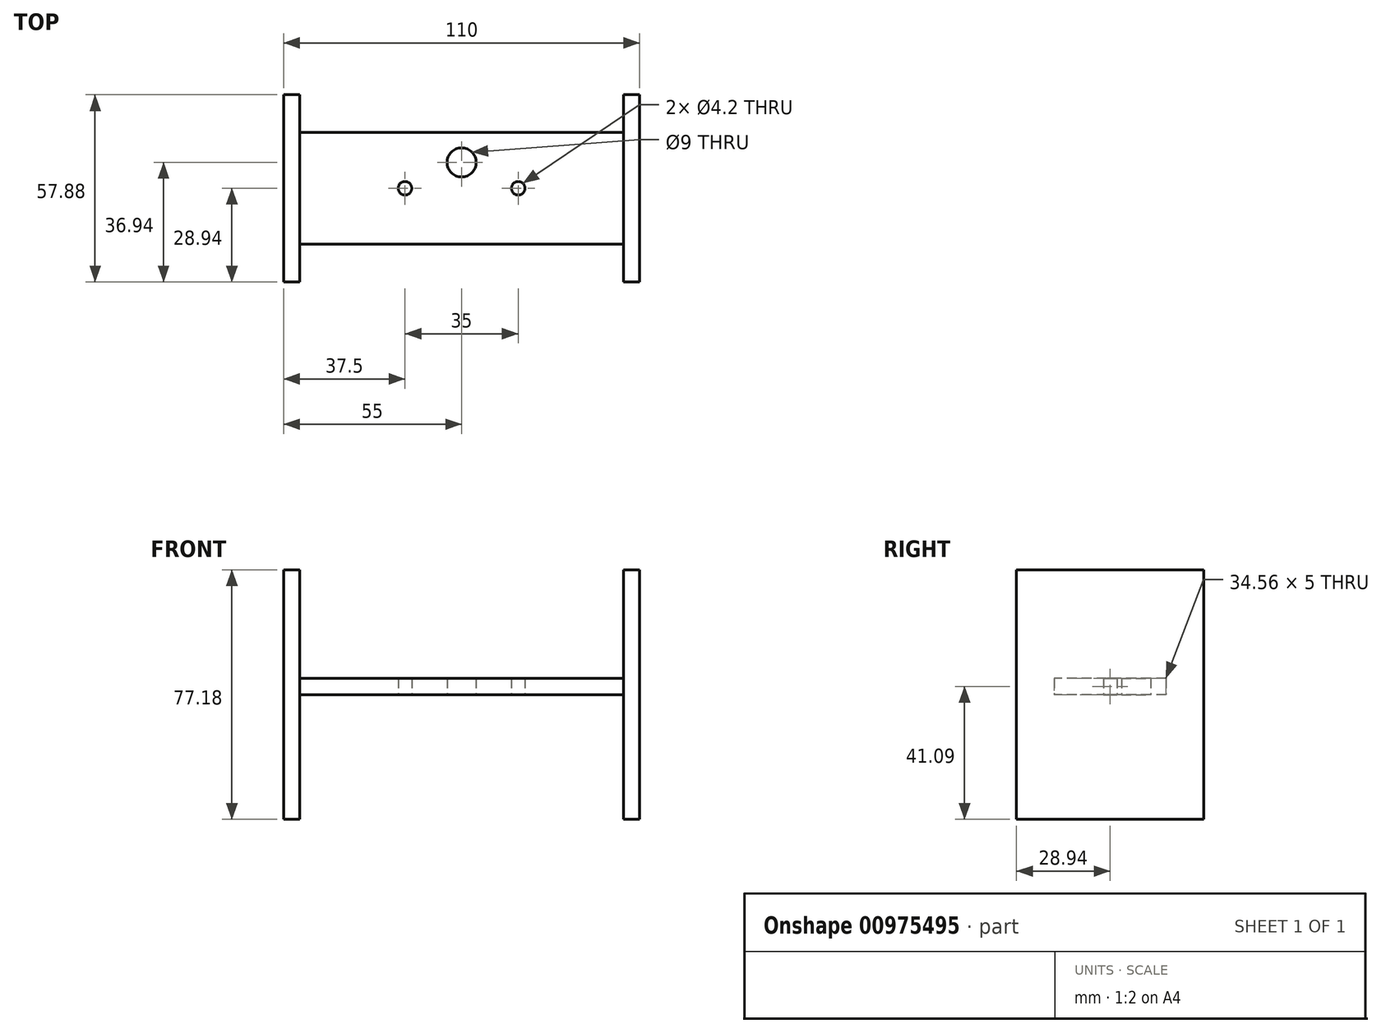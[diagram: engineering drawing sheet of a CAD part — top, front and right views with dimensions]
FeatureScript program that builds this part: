
annotation { "Feature Type Name" : "Feature", "Feature Type Description" : "" }
export const myFeature = defineFeature(function(context is Context, id is Id, definition is map)
    precondition{}
    {
        {
            var Q0;
            Q0=qCreatedBy(makeId("Top.planeOp"),FACE);
            var sketch = newSketch(context, id + "F0", { "sketchPlane" : qUnion([Q0])});
            skLineSegment(sketch, "E0.bottom", {"start": v(50, 17.28) * mm, "end": v(-50, 17.28) * mm});
            skLineSegment(sketch, "E0.top", {"start": v(50, -17.28) * mm, "end": v(-50, -17.28) * mm});
            skLineSegment(sketch, "E0.left", {"start": v(50, 17.28) * mm, "end": v(50, 12.28) * mm});
            skLineSegment(sketch, "E0.right", {"start": v(-50, 17.28) * mm, "end": v(-50, 12.28) * mm});
            skPoint(sketch, "E0.middle", {"position": v(0, 0) * mm});
            skLineSegment(sketch, "E1.bottom", {"start": v(55, -12.28) * mm, "end": v(50, -12.28) * mm});
            skLineSegment(sketch, "E1.top", {"start": v(55, 12.28) * mm, "end": v(50, 12.28) * mm});
            skLineSegment(sketch, "E1.left", {"start": v(55, -12.28) * mm, "end": v(55, 12.28) * mm});
            skPoint(sketch, "E1.middle", {"position": v(50, 0) * mm});
            skPoint(sketch, "E2.orphan", {"position": v(45, 12.28) * mm});
            skLineSegment(sketch, "E3.trimOffspring", {"start": v(50, -12.28) * mm, "end": v(50, -17.28) * mm});
            skPoint(sketch, "E4.orphan", {"position": v(45, -12.28) * mm});
            skLineSegment(sketch, "E5.MirrorCS", {"start": v(-55, 12.28) * mm, "end": v(-50, 12.28) * mm});
            skLineSegment(sketch, "E6.MirrorCS", {"start": v(-55, -12.28) * mm, "end": v(-55, 12.28) * mm});
            skLineSegment(sketch, "E7.MirrorCS", {"start": v(-55, -12.28) * mm, "end": v(-50, -12.28) * mm});
            skLineSegment(sketch, "E8.trimOffspring", {"start": v(-50, -12.28) * mm, "end": v(-50, -17.28) * mm});
            skCircle(sketch, "E9", {"center": v(17.5, 0) * mm, "radius": 2.1 * mm});
            skCircle(sketch, "E10.MirrorC", {"center": v(-17.5, 0) * mm, "radius": 2.1 * mm});
            skCircle(sketch, "E11", {"center": v(0, 8) * mm, "radius": 4.5 * mm});
            skSolve(sketch);
        }
        {
            var Q0;
            Q0=makeQuery(id+"F0.imprint","IMPRINT",FACE,{"disambiguationData":[TD([[makeQuery(id+"F0.imprint","IMPRINT",EDGE,{"derivedFrom":sQuery(id+"F0.wireOp",EDGE,"E0.bottom")}),1.0]])]});
            extrude(context, id + "F1", {"entities" : qUnion([Q0]), "depth" : 5 * mm, "offsetDistance" : 25 * mm});
        }
        {
            var Q0;
            Q0=makeQuery(id+"F1.opExtrude","SWEPT_FACE",FACE,{"disambiguationData":[OSD([sQuery(id+"F0.wireOp",EDGE,"E1.left")])]});
            cPlane(context, id + "F2", {"entities" : qUnion([Q0]), "cplaneType" : CPlaneType.OFFSET, "offset" : 0 * mm, "width" : 150 * mm, "height" : 150 * mm});
        }
        {
            var Q0;
            Q0=qCreatedBy(id+"F2.planeOp",FACE);
            var sketch = newSketch(context, id + "F3", { "sketchPlane" : qUnion([Q0])});
            skLineSegment(sketch, "E12.bottom", {"start": v(28.94, -38.6) * mm, "end": v(-28.94, -38.6) * mm});
            skLineSegment(sketch, "E12.top", {"start": v(28.94, 38.6) * mm, "end": v(-28.94, 38.6) * mm});
            skLineSegment(sketch, "E12.left", {"start": v(28.94, -38.6) * mm, "end": v(28.94, 38.6) * mm});
            skLineSegment(sketch, "E12.right", {"start": v(-28.94, -38.6) * mm, "end": v(-28.94, 38.6) * mm});
            skPoint(sketch, "E12.middle", {"position": v(0, 0) * mm});
            skSolve(sketch);
        }
        {
            var Q0;
            Q0=makeQuery(id+"F3.imprint","IMPRINT",FACE,{"disambiguationData":[TD([[makeQuery(id+"F3.imprint","IMPRINT",EDGE,{"derivedFrom":sQuery(id+"F3.wireOp",EDGE,"E12.bottom")}),-1.0]])]});
            extrude(context, id + "F4", {"entities" : qUnion([Q0]), "operationType" : NewBodyOperationType.ADD, "depth" : -5 * mm, "offsetDistance" : 25 * mm});
        }
        {
            var Q0;
            Q0=makeQuery(id+"F1.opExtrude","SWEPT_BODY",BODY,{"disambiguationData":[OSD([sQuery(id+"F0.wireOp",EDGE,"E0.bottom"),sQuery(id+"F0.wireOp",EDGE,"E0.top"),sQuery(id+"F0.wireOp",EDGE,"E0.left"),sQuery(id+"F0.wireOp",EDGE,"E0.right"),sQuery(id+"F0.wireOp",EDGE,"E1.bottom"),sQuery(id+"F0.wireOp",EDGE,"E1.top"),sQuery(id+"F0.wireOp",EDGE,"E1.left"),sQuery(id+"F0.wireOp",EDGE,"E3.trimOffspring"),sQuery(id+"F0.wireOp",EDGE,"E5.MirrorCS"),sQuery(id+"F0.wireOp",EDGE,"E6.MirrorCS"),sQuery(id+"F0.wireOp",EDGE,"E7.MirrorCS"),sQuery(id+"F0.wireOp",EDGE,"E8.trimOffspring"),sQuery(id+"F0.wireOp",EDGE,"E9"),sQuery(id+"F0.wireOp",EDGE,"E10.MirrorC"),sQuery(id+"F0.wireOp",EDGE,"E11")])]});
            var Q1;
            Q1=qCreatedBy(makeId("Right.planeOp"),FACE);
            mirror(context, id + "F5", {"operationType" : NewBodyOperationType.ADD, "entities" : qUnion([Q0]), "mirrorPlane" : qUnion([Q1])});
        }
    });
